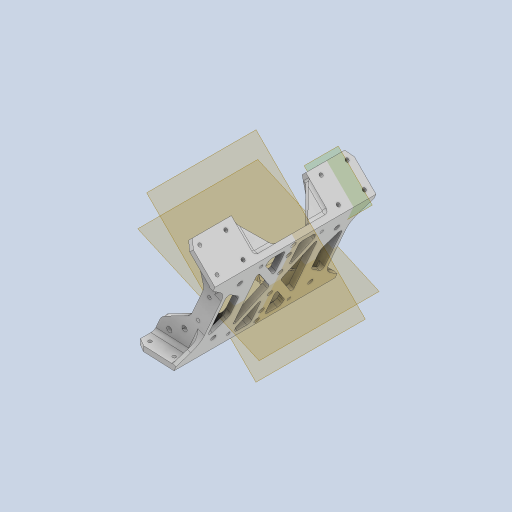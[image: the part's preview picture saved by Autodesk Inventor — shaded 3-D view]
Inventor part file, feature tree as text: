
AUTODESK INVENTOR PART (.ipt)
format: ipt  version: 2023 (Build 270158000, 158)  size: 1,319,424 bytes
history: native  units: mm
features: projected_geometry x33, sketch x22, extrude x20, fillet x13, mirror x9, reference x6, other x6, plane x5, chamfer x4, hole x2
ambient origin geometry x8: Origin, YZ Plane, XZ Plane, XY Plane, X Axis, Y Axis, Z Axis, Center Point
bodies: Solid1 (feature_tree)
feature tree (120):
  sketch  "Sketch1"  dims[d1=3.0mm d2=22.0mm]
  plane  "Work Plane1"
  extrude  "Extrusion1"  Depth=22.0mm
  hole  "Hole1"  [1 undecoded]
  hole  "Hole2"  [1 undecoded]
  sketch  "Sketch4"  dims[d8=2.0mm d9=6.0mm d10=4.0mm d11=2.0mm d12=90.0deg d13=20.0mm d14=0.0mm]
  plane  "Work Plane2"
  extrude  "Extrusion2"  Depth=10.0mm
  plane  "Work Plane3"
  mirror  "Mirror1"
  extrude  "Extrusion3"  Depth=10.0mm TaperAngle=0.0deg
  mirror  "Mirror2"
  extrude  "Extrusion4"  Depth=15.0mm
  extrude  "Extrusion5"  Depth=18.0mm
  plane  "Work Plane4"
  mirror  "Mirror3"
  fillet  "Fillet1"  Radius=18.0mm
  fillet  "Fillet6"  Radius=2.0mm
  extrude  "Extrusion7"  Depth=2.0mm
  extrude  "Extrusion8"  Depth=7.0mm
  extrude  "Extrusion9"  Depth=7.0mm
  extrude  "Extrusion10"  Depth=3.0mm
  mirror  "Mirror4"
  mirror  "Mirror5"
  extrude  "Extrusion11"  Depth=3.0mm
  extrude  "Extrusion12"  Depth=35.0mm
  extrude  "Extrusion13"  Depth=3.0mm
  extrude  "Extrusion14"  Depth=3.0mm
  extrude  "Extrusion15"  Depth=20.0mm TaperAngle=0.0deg
  mirror  "Mirror6"
  extrude  "Extrusion16"  Depth=2.5mm
  mirror  "Mirror7"
  plane  "Work Plane5"
  extrude  "Extrusion17"  Depth=2.5mm
  mirror  "Mirror8"
  chamfer  "Chamfer2"  Distance=2.0mm
  chamfer  "Chamfer3"  Distance=1.0mm
  chamfer  "Chamfer4"  Distance=20.0mm
  chamfer  "Chamfer5"  Angle=30.0deg  [1 undecoded]
  fillet  "Fillet7"  Radius=5.0mm
  fillet  "Fillet8"  Radius=4.0mm
  fillet  "Fillet9"  Radius=4.0mm
  fillet  "Fillet10"  Radius=1.0mm
  fillet  "Fillet11"  Radius=2.0mm
  fillet  "Fillet12"  Radius=20.0mm
  extrude  "Extrusion18"  Depth=12.0mm
  extrude  "Extrusion19"  Depth=12.0mm
  extrude  "Extrusion20"  Depth=12.0mm
  fillet  "Fillet13"  Radius=3.0mm
  fillet  "Fillet14"  Radius=20.0mm
  extrude  "Extrusion21"  Depth=12.0mm TaperAngle=0.0deg
  mirror  "Mirror9"
  fillet  "Fillet15"  Radius=15.0mm
  fillet  "Fillet16"  Radius=15.0mm
  fillet  "Fillet17"  Radius=15.0mm
  reference  "Reference1"
  reference  "Reference2"
  sketch  "Sketch2"  dims[d4=3.0mm d5=22.0mm]
  reference  "Reference3"
  reference  "Reference4"
  sketch  "Sketch3"  dims[d6=10.0mm d7=0.0mm]
  reference  "Reference5"
  reference  "Reference6"
  projected_geometry  "Projected Loop1"
  projected_geometry  "Projected Loop2"
  sketch  "Sketch5"  dims[d15=2.0mm d16=6.0mm d17=4.0mm d18=2.0mm d19=90.0deg d20=20.0mm d21=0.0mm d22=3.0mm]
  projected_geometry  "Projected Loop3"
  projected_geometry  "Projected Loop4"
  sketch  "Sketch6"  dims[d23=10.0mm d24=0.0mm d25=10.0mm]
  projected_geometry  "Projected Loop5"
  projected_geometry  "Projected Loop6"
  projected_geometry  "Projected Loop7"
  projected_geometry  "Projected Loop8"
  projected_geometry  "Projected Loop9"
  sketch  "Sketch7"  dims[d26=10.0mm d27=2.0mm d28=0.0mm]
  projected_geometry  "Projected Loop10"
  projected_geometry  "Projected Loop11"
  projected_geometry  "Projected Loop12"
  projected_geometry  "Projected Loop13"
  projected_geometry  "Projected Loop14"
  sketch  "Sketch9"  dims[d29=2.0mm d30=0.0mm d31=15.0mm]
  projected_geometry  "Projected Loop16"
  sketch  "Sketch10"  dims[d32=15.0mm d33=18.0mm d34=18.0mm d35=2.0mm d36=0.0mm]
  projected_geometry  "Projected Loop17"
  sketch  "Sketch11"  dims[d40=2.0mm d53=2.0mm]
  projected_geometry  "Projected Loop18"
  sketch  "Sketch12"  dims[d54=4.0mm d55=7.0mm]
  projected_geometry  "Projected Loop19"
  sketch  "Sketch13"  dims[d56=4.0mm d57=7.0mm]
  projected_geometry  "Projected Loop20"
  sketch  "Sketch14"  dims[d58=3.0mm d59=3.0mm]
  projected_geometry  "Projected Loop21"
  projected_geometry  "Projected Loop22"
  sketch  "Sketch15"  dims[d60=3.0mm d61=3.0mm]
  projected_geometry  "Projected Loop23"
  projected_geometry  "Projected Loop24"
  sketch  "Sketch16"  dims[d62=500.0mm d63=0.0mm d64=35.0mm]
  projected_geometry  "Projected Loop25"
  sketch  "Sketch17"  dims[d65=47.0mm d66=3.0mm]
  projected_geometry  "Projected Loop26"
  sketch  "Sketch18"  dims[d67=3.0mm d68=3.0mm]
  projected_geometry  "Projected Loop27"
  projected_geometry  "Projected Loop28"
  sketch  "Sketch20"  dims[d69=3.0mm d70=20.0mm d71=0.0mm]
  projected_geometry  "Projected Loop29"
  projected_geometry  "Projected Loop30"
  sketch  "Sketch21"  dims[d72=4.0mm d73=2.5mm]
  projected_geometry  "Projected Loop31"
  sketch  "Sketch22"  dims[d74=2.5mm d75=2.5mm]
  projected_geometry  "Projected Loop32"
  sketch  "Sketch23"  dims[d76=2.5mm]
  projected_geometry  "Projected Loop33"
  sketch  "Sketch24"  dims[d78=4.0mm d79=2.0mm d80=1.0mm d81=20.0mm d82=0.0mm d83=30.0deg d84=5.0mm d85=4.0mm d86=4.0mm d87=1.0mm d88=2.0mm d89=20.0mm d90=0.0mm d91=12.0mm d92=12.0mm d93=3.0mm d94=3.0mm d95=20.0mm d96=0.0mm d97=15.0mm d98=0.0mm d99=15.0mm d100=0.0mm d101=15.0mm d102=15.0mm d103=2.0mm d104=2.0mm d105=20.0mm d106=0.0mm d107=15.0mm d108=15.0mm d109=2.0mm d110=2.0mm d111=20.0mm d112=0.0mm d113=20.0mm d114=20.0mm d115=20.0mm d116=0.0mm d117=-13.0mm d118=2.5mm d119=0.0mm d128=2.5mm d129=2.0mm d130=60.0deg d131=2.5mm d132=2.0mm d133=60.0deg d134=2.5mm d135=2.0mm d136=60.0deg d137=2.5mm d138=2.0mm d139=60.0deg d140=4.0mm d141=1.5mm d142=1.5mm d143=20.0mm d144=2.0mm d145=1.5mm d146=56.0mm d147=38.0mm d148=3.0mm d149=3.0mm d150=3.0mm d151=3.0mm d152=4.0mm d153=0.0mm d154=2.0mm d155=2.0mm d156=2.0mm d157=2.0mm d158=4.0mm d159=0.0mm d160=10.0mm d161=10.0mm d162=12.0mm d163=12.0mm d164=15.0mm d165=15.0mm d166=300.0mm d167=0.0mm d168=6.0mm d169=6.0mm d170=3.0mm d171=3.0mm d172=10.0mm d173=3.0mm d174=10.0mm d175=3.0mm d176=4.0mm d177=4.0mm d178=8.0mm d179=8.0mm d180=2.0mm d181=2.0mm d182=8.0mm d183=0.0mm d184=2.0mm d185=1.0mm d186=12.0mm]
  projected_geometry  "Projected Loop34"
  parser-record x1  (decoder bookkeeping rows leaked as tree rows — omitted from the tree; the rows remain in map.json)
  other  "body_8d_1.iam"
  other  "leg_1_2d_MIR:2"
  other  "leg_holder_2_MIR:1"
  other  "leg_2d_1:1"
  other  "leg_holder_2:1"
note: 3 required parameter values undecoded (feature->parameter linkage not recoverable at this tier; creation-order binding heuristic only, values carry confidence <= 0.55)
note: 1 file-system path scrubbed to <path> (originals preserved in map.json)
